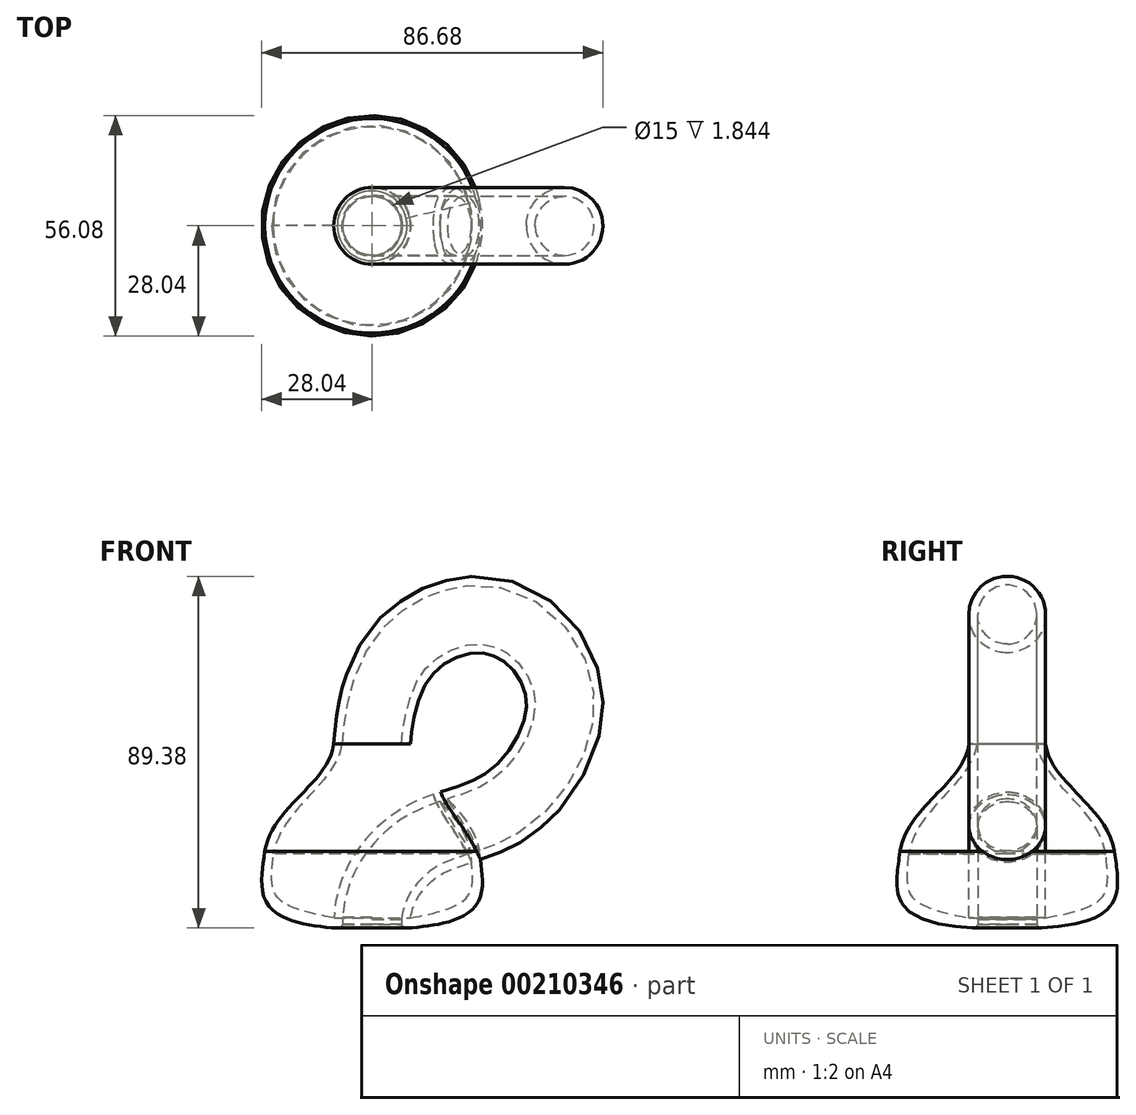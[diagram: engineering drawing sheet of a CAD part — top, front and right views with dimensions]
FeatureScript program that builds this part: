
annotation { "Feature Type Name" : "Feature", "Feature Type Description" : "" }
export const myFeature = defineFeature(function(context is Context, id is Id, definition is map)
    precondition{}
    {
        {
            var Q0;
            Q0=qCreatedBy(makeId("Top.planeOp"),FACE);
            cPlane(context, id + "F0", {"entities" : qUnion([Q0]), "cplaneType" : CPlaneType.OFFSET, "offset" : 10 * mm, "width" : 150 * mm, "height" : 150 * mm});
        }
        {
            var Q0;
            Q0=qCreatedBy(makeId("Front.planeOp"),FACE);
            var sketch = newSketch(context, id + "F1", { "sketchPlane" : qUnion([Q0])});
            skFitSpline(sketch, "E0", {"points": [v(0, -37) * mm, v(-27.27, -17.3) * mm], "startDerivative": vector(-94.05, 0) * mm, "endDerivative": vector(4.36, 34.9) * mm});
            skFitSpline(sketch, "E1", {"points": [v(-27.27, -17.3) * mm, v(-9.75, 10) * mm], "startDerivative": vector(6, 34.9) * mm, "endDerivative": vector(3.9, 30) * mm});
            skLineSegment(sketch, "E2", {"start": v(0, 29.27) * mm, "end": v(0, -41.64) * mm});
            skFitSpline(sketch, "E3", {"points": [v(0, -35.5) * mm, v(-25.1, -17.93) * mm], "startDerivative": vector(-83.42, 10.41) * mm, "endDerivative": vector(2.7, 33.94) * mm});
            skFitSpline(sketch, "E4", {"points": [v(-25.1, -17.93) * mm, v(-7.75, 10) * mm], "startDerivative": vector(6, 34.9) * mm, "endDerivative": vector(3.82, 30) * mm});
            skLineSegment(sketch, "E5", {"start": v(0, 10) * mm, "end": v(-9.75, 10) * mm});
            skLineSegment(sketch, "E6", {"start": v(0, -37) * mm, "end": v(-31.35, -37) * mm});
            skFitSpline(sketch, "E7", {"points": [v(0, 10) * mm, v(6.55, 32.26) * mm, v(32.3, 42.22) * mm, v(48.88, 21.04) * mm, v(33.93, -5.78) * mm, v(12.35, -14.86) * mm, v(0, -35.5) * mm], "startDerivative": vector(5.14, 79.93) * mm, "endDerivative": vector(0, -162.5) * mm});
            skSolve(sketch);
        }
        {
            var Q0;
            {var subQ2=sQuery(id+"F1.wireOp",EDGE,"E0");Q0=makeQuery(id+"F1.imprint","IMPRINT",FACE,{"disambiguationData":[TD([[makeQuery(id+"F1.imprint","IMPRINT",EDGE,{"derivedFrom":subQ2}),-1.0]])]});}
            var Q1;
            Q1=sQuery(id+"F1.wireOp",EDGE,"E2");
            revolve(context, id + "F2", {"entities" : qUnion([Q0]), "axis" : qUnion([Q1]), "revolveType" : RevolveType.FULL});
        }
        {
            var Q0;
            Q0=qCreatedBy(id+"F0.planeOp",FACE);
            var sketch = newSketch(context, id + "F3", { "sketchPlane" : qUnion([Q0])});
            skCircle(sketch, "E8", {"center": v(0, 0) * mm, "radius": 7.5 * mm});
            skCircle(sketch, "E9", {"center": v(0, 0) * mm, "radius": 9.5 * mm});
            skSolve(sketch);
        }
        {
            var Q0;
            Q0=makeQuery(id+"F2.opRevolve","SWEPT_FACE",FACE,{"disambiguationData":[OSD([sQuery(id+"F1.wireOp",EDGE,"E5")])]});
            var Q1;
            Q1 = qSketchRegion(id + "F3", true);
            var Q2;
            Q2=sQuery(id+"F1.wireOp",EDGE,"E7");
            sweep(context, id + "F4", {"operationType" : NewBodyOperationType.ADD, "profiles" : qUnion([Q0, Q1]), "path" : qUnion([Q2])});
        }
        {
            var Q0;
            Q0=qCreatedBy(makeId("Top.planeOp"),FACE);
            cPlane(context, id + "F5", {"entities" : qUnion([Q0]), "cplaneType" : CPlaneType.OFFSET, "offset" : 37 * mm, "oppositeDirection" : true, "width" : 150 * mm, "height" : 150 * mm});
        }
        {
            var Q0;
            Q0=qCreatedBy(id+"F5.planeOp",FACE);
            var sketch = newSketch(context, id + "F6", { "sketchPlane" : qUnion([Q0])});
            skCircle(sketch, "E10", {"center": v(0, 0) * mm, "radius": 7.5 * mm});
            skSolve(sketch);
        }
        {
            var Q0;
            Q0=makeQuery(id+"F6.imprint","IMPRINT",FACE,{"disambiguationData":[TD([[makeQuery(id+"F6.imprint","IMPRINT",EDGE,{"derivedFrom":sQuery(id+"F6.wireOp",EDGE,"E10")}),1.0]])]});
            extrude(context, id + "F7", {"entities" : qUnion([Q0]), "operationType" : NewBodyOperationType.REMOVE, "depth" : 3 * mm});
        }
        {
            var Q0;
            Q0=qCreatedBy(makeId("Front.planeOp"),FACE);
            var sketch = newSketch(context, id + "F8", { "sketchPlane" : qUnion([Q0])});
            skArc(sketch, "E11", {"start": v(-8.87, -36.72) * mm, "mid": v(-7.93, -36.46) * mm, "end": v(-7.45, -35.62) * mm});
            skLineSegment(sketch, "E12", {"start": v(0, -37.54) * mm, "end": v(-7.5, -37.54) * mm, "construction": true});
            skLineSegment(sketch, "E13", {"start": v(-7.5, -37.54) * mm, "end": v(-7.5, -33.4) * mm, "construction": true});
            skLineSegment(sketch, "E14", {"start": v(-7.45, -35.62) * mm, "end": v(-5.1, -36.25) * mm});
            skLineSegment(sketch, "E15", {"start": v(-5.1, -36.25) * mm, "end": v(-7.7, -39.12) * mm});
            skLineSegment(sketch, "E16", {"start": v(-7.7, -39.12) * mm, "end": v(-8.87, -36.72) * mm});
            skSolve(sketch);
        }
        {
            var Q0;
            Q0=makeQuery(id+"F8.imprint","IMPRINT",FACE,{"disambiguationData":[TD([[makeQuery(id+"F8.imprint","IMPRINT",EDGE,{"derivedFrom":sQuery(id+"F8.wireOp",EDGE,"E11")}),-1.0]])]});
            var Q1;
            Q1=sQuery(id+"F1.wireOp",EDGE,"E2");
            revolve(context, id + "F9", {"operationType" : NewBodyOperationType.REMOVE, "entities" : qUnion([Q0]), "axis" : qUnion([Q1]), "revolveType" : RevolveType.FULL, "oppositeDirection" : true});
        }
    });
